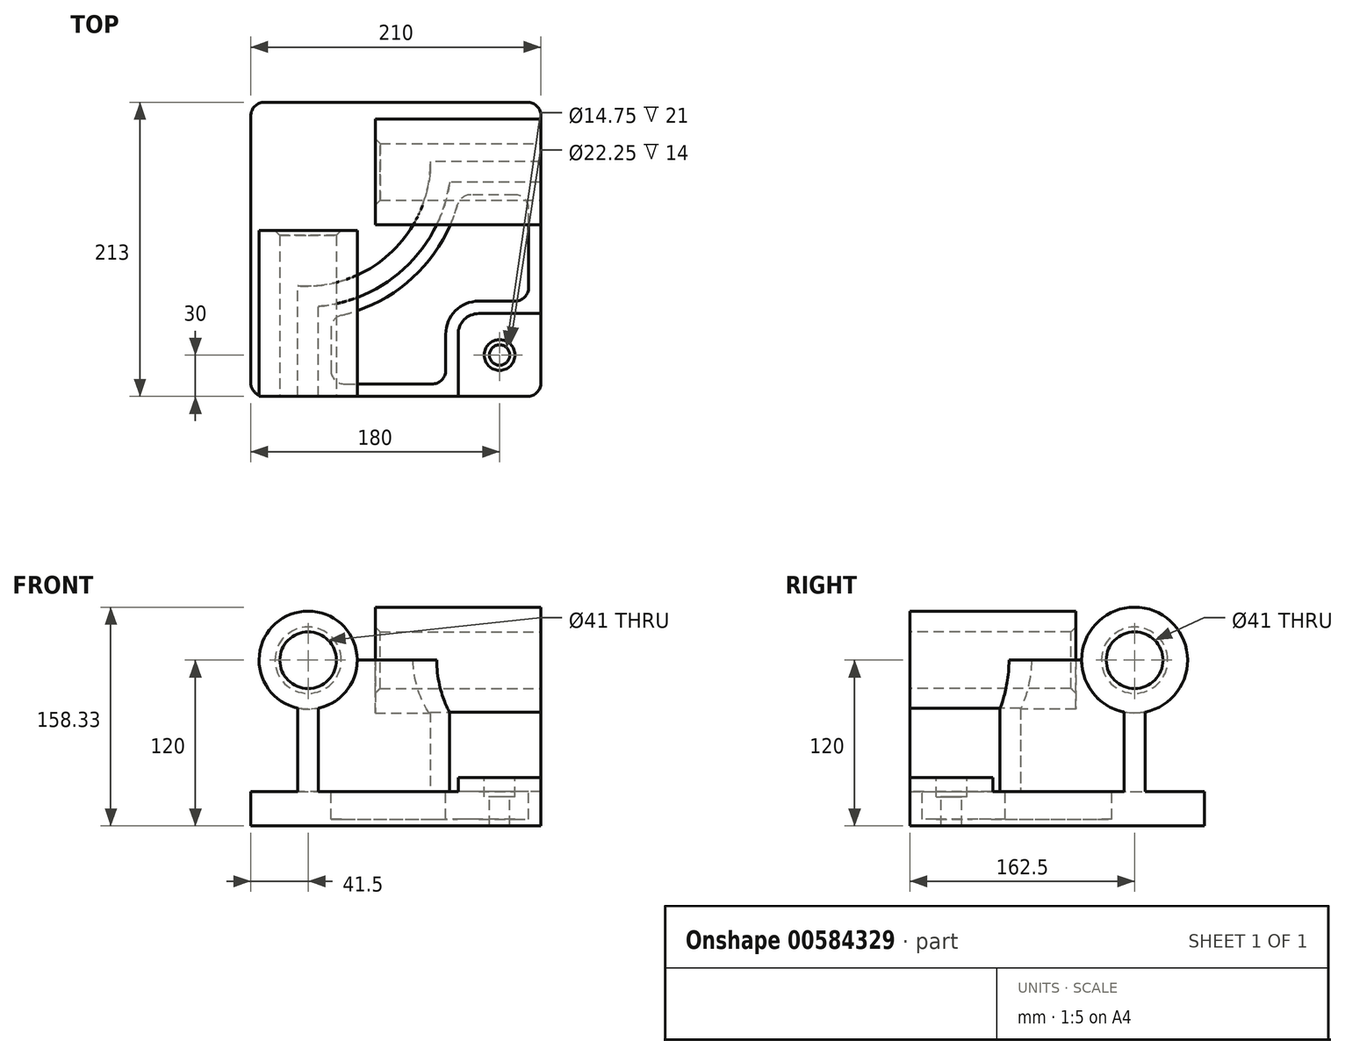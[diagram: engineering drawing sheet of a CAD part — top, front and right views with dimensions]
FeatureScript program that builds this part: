
annotation { "Feature Type Name" : "Feature", "Feature Type Description" : "" }
export const myFeature = defineFeature(function(context is Context, id is Id, definition is map)
    precondition{}
    {
        {
            var Q0;
            Q0=qCreatedBy(makeId("Top.planeOp"),FACE);
            var sketch = newSketch(context, id + "F0", { "sketchPlane" : qUnion([Q0])});
            skLineSegment(sketch, "E0.bottom", {"start": v(105, -106.5) * mm, "end": v(-105, -106.5) * mm});
            skLineSegment(sketch, "E0.top", {"start": v(105, 106.5) * mm, "end": v(-105, 106.5) * mm});
            skLineSegment(sketch, "E0.left", {"start": v(105, -106.5) * mm, "end": v(105, 106.5) * mm});
            skLineSegment(sketch, "E0.right", {"start": v(-105, -106.5) * mm, "end": v(-105, 106.5) * mm});
            skPoint(sketch, "E0.middle", {"position": v(0, 0) * mm});
            skSolve(sketch);
        }
        {
            var Q0;
            Q0=makeQuery(id+"F0.imprint","IMPRINT",FACE,{"disambiguationData":[TD([[makeQuery(id+"F0.imprint","IMPRINT",EDGE,{"derivedFrom":sQuery(id+"F0.wireOp",EDGE,"E0.bottom")}),-1.0]])]});
            extrude(context, id + "F1", {"entities" : qUnion([Q0]), "depth" : 25 * mm, "offsetDistance" : 25 * mm});
        }
        {
            var Q0;
            Q0=makeQuery(id+"F1.opExtrude","CAP_FACE",FACE,{"disambiguationData":[OSD([sQuery(id+"F0.wireOp",EDGE,"E0.bottom"),sQuery(id+"F0.wireOp",EDGE,"E0.top"),sQuery(id+"F0.wireOp",EDGE,"E0.left"),sQuery(id+"F0.wireOp",EDGE,"E0.right")])],"isStart":false});
            var sketch = newSketch(context, id + "F2", { "sketchPlane" : qUnion([Q0])});
            skLineSegment(sketch, "E1", {"start": v(-71, -106.5) * mm, "end": v(-71, -26.5) * mm});
            skLineSegment(sketch, "E2", {"start": v(105, 63.5) * mm, "end": v(25, 63.5) * mm});
            skArc(sketch, "E3", {"start": v(-71, -26.5) * mm, "mid": v(-3.5, -2.3) * mm, "end": v(25, 63.5) * mm});
            skLineSegment(sketch, "E4", {"start": v(25, 63.5) * mm, "end": v(-65.19, 63.5) * mm, "construction": true});
            skLineSegment(sketch, "E5", {"start": v(-71, -26.5) * mm, "end": v(-65.19, 63.5) * mm, "construction": true});
            skLineSegment(sketch, "E6.0", {"start": v(-56, -106.5) * mm, "end": v(-56, -41.29) * mm});
            skArc(sketch, "E6.1", {"start": v(-56, -41.29) * mm, "mid": v(7.1, -12.92) * mm, "end": v(38.92, 48.5) * mm});
            skLineSegment(sketch, "E6.2", {"start": v(105, 48.5) * mm, "end": v(38.92, 48.5) * mm});
            skSolve(sketch);
        }
        {
            var Q0;
            {var subQ4=sQuery(id+"F2.wireOp",EDGE,"E1");Q0=makeQuery(id+"F2.imprint","IMPRINT",FACE,{"disambiguationData":[TD([[makeQuery(id+"F2.imprint","IMPRINT",EDGE,{"derivedFrom":subQ4}),-1.0]])]});}
            extrude(context, id + "F3", {"entities" : qUnion([Q0]), "operationType" : NewBodyOperationType.ADD, "depth" : 95 * mm, "offsetDistance" : 25 * mm});
        }
        {
            var Q0;
            {var subQ0=sQuery(id+"F0.wireOp",EDGE,"E0.bottom");Q0=makeQuery(id+"F3.boolean.opBoolean","MERGE",FACE,{"derivedFrom":[makeQuery(id+"F1.opExtrude","SWEPT_FACE",FACE,{"disambiguationData":[OSD([subQ0])]}),makeQuery(id+"F3.opExtrude","SWEPT_FACE",FACE,{"disambiguationData":[OSD([subQ0])]})]});}
            var sketch = newSketch(context, id + "F4", { "sketchPlane" : qUnion([Q0])});
            skCircle(sketch, "E7", {"center": v(-63.5, 120) * mm, "radius": 35.5 * mm});
            skSolve(sketch);
        }
        {
            var Q0;
            Q0 = qSketchRegion(id + "F4", true);
            extrude(context, id + "F5", {"entities" : qUnion([Q0]), "operationType" : NewBodyOperationType.ADD, "depth" : 0 * mm, "offsetDistance" : 25 * mm, "hasSecondDirection" : true, "secondDirectionOppositeDirection" : true, "secondDirectionDepth" : 120 * mm});
        }
        {
            var Q0;
            {var subQ0=sQuery(id+"F0.wireOp",EDGE,"E0.left");Q0=makeQuery(id+"F3.boolean.opBoolean","MERGE",FACE,{"derivedFrom":[makeQuery(id+"F1.opExtrude","SWEPT_FACE",FACE,{"disambiguationData":[OSD([subQ0])]}),makeQuery(id+"F3.opExtrude","SWEPT_FACE",FACE,{"disambiguationData":[OSD([subQ0])]})]});}
            var sketch = newSketch(context, id + "F6", { "sketchPlane" : qUnion([Q0])});
            skCircle(sketch, "E8", {"center": v(56, 120) * mm, "radius": 38.33 * mm});
            skSolve(sketch);
        }
        {
            var Q0;
            Q0 = qSketchRegion(id + "F6", true);
            extrude(context, id + "F7", {"entities" : qUnion([Q0]), "operationType" : NewBodyOperationType.ADD, "depth" : 0 * mm, "offsetDistance" : 25 * mm, "hasSecondDirection" : true, "secondDirectionOppositeDirection" : true, "secondDirectionDepth" : 120 * mm});
        }
        {
            var Q0;
            {var subQ0=sQuery(id+"F0.wireOp",EDGE,"E0.left");var subQ1=sQuery(id+"F0.wireOp",EDGE,"E0.bottom");Q0=makeQuery(id+"F3.boolean.opBoolean","SPLIT",FACE,{"disambiguationData":[TD([makeQuery(id+"F3.opExtrude","SWEPT_FACE",FACE,{"disambiguationData":[OSD([sQuery(id+"F2.wireOp",EDGE,"E6.0")])]})])],"derivedFrom":makeQuery(id+"F1.opExtrude","CAP_FACE",FACE,{"disambiguationData":[OSD([subQ1,sQuery(id+"F0.wireOp",EDGE,"E0.top"),subQ0,sQuery(id+"F0.wireOp",EDGE,"E0.right")])],"isStart":false})});}
            var sketch = newSketch(context, id + "F8", { "sketchPlane" : qUnion([Q0])});
            skLineSegment(sketch, "E9.bottom", {"start": v(105, -106.5) * mm, "end": v(45, -106.5) * mm});
            skLineSegment(sketch, "E9.top", {"start": v(105, -46.5) * mm, "end": v(45, -46.5) * mm});
            skLineSegment(sketch, "E9.left", {"start": v(105, -106.5) * mm, "end": v(105, -46.5) * mm});
            skLineSegment(sketch, "E9.right", {"start": v(45, -106.5) * mm, "end": v(45, -46.5) * mm});
            skSolve(sketch);
        }
        {
            var Q0;
            Q0 = qSketchRegion(id + "F8", true);
            extrude(context, id + "F9", {"entities" : qUnion([Q0]), "operationType" : NewBodyOperationType.ADD, "depth" : 10 * mm, "offsetDistance" : 25 * mm});
        }
        {
            var Q0;
            Q0=makeQuery(id+"F9.opExtrude","SWEPT_EDGE",EDGE,{"disambiguationData":[OSD([sQuery(id+"F8.wireOp",EDGE,"E9.top"),sQuery(id+"F8.wireOp",EDGE,"E9.right")])]});
            fillet(context, id + "F10", {"entities" : qUnion([Q0]), "radius" : 15 * mm, "tangentPropagation" : true, "allowEdgeOverflow" : false});
        }
        {
            var Q0;
            {var subQ0=sQuery(id+"F0.wireOp",EDGE,"E0.left");var subQ1=sQuery(id+"F0.wireOp",EDGE,"E0.bottom");Q0=makeQuery(id+"F3.boolean.opBoolean","SPLIT",FACE,{"disambiguationData":[TD([makeQuery(id+"F3.opExtrude","SWEPT_FACE",FACE,{"disambiguationData":[OSD([sQuery(id+"F2.wireOp",EDGE,"E6.0")])]})])],"derivedFrom":makeQuery(id+"F1.opExtrude","CAP_FACE",FACE,{"disambiguationData":[OSD([subQ1,sQuery(id+"F0.wireOp",EDGE,"E0.top"),subQ0,sQuery(id+"F0.wireOp",EDGE,"E0.right")])],"isStart":false})});}
            var sketch = newSketch(context, id + "F11", { "sketchPlane" : qUnion([Q0])});
            skLineSegment(sketch, "E10.0", {"start": v(-47, -49.23) * mm, "end": v(-47, -97.5) * mm});
            skArc(sketch, "E10.1", {"start": v(46.45, 39.5) * mm, "mid": v(13.44, -19.3) * mm, "end": v(-47, -49.23) * mm});
            skLineSegment(sketch, "E10.2", {"start": v(-47, -97.5) * mm, "end": v(36, -97.5) * mm});
            skLineSegment(sketch, "E10.3", {"start": v(96, 39.5) * mm, "end": v(46.45, 39.5) * mm});
            skLineSegment(sketch, "E10.4", {"start": v(36, -97.5) * mm, "end": v(36, -61.5) * mm});
            skArc(sketch, "E10.5", {"start": v(36, -61.5) * mm, "mid": v(43.03, -44.53) * mm, "end": v(60, -37.5) * mm});
            skLineSegment(sketch, "E10.6", {"start": v(60, -37.5) * mm, "end": v(96, -37.5) * mm});
            skLineSegment(sketch, "E10.7", {"start": v(96, -37.5) * mm, "end": v(96, 39.5) * mm});
            skSolve(sketch);
        }
        {
            var Q0;
            Q0=makeQuery(id+"F11.imprint","IMPRINT",FACE,{"disambiguationData":[TD([[makeQuery(id+"F11.imprint","IMPRINT",EDGE,{"derivedFrom":sQuery(id+"F11.wireOp",EDGE,"E10.0")}),1.0]])]});
            extrude(context, id + "F12", {"entities" : qUnion([Q0]), "operationType" : NewBodyOperationType.REMOVE, "oppositeDirection" : true, "depth" : 20 * mm, "offsetDistance" : 25 * mm});
        }
        {
            var Q0;
            Q0=makeQuery(id+"F9.opExtrude","CAP_FACE",FACE,{"disambiguationData":[OSD([sQuery(id+"F8.wireOp",EDGE,"E9.bottom"),sQuery(id+"F8.wireOp",EDGE,"E9.top"),sQuery(id+"F8.wireOp",EDGE,"E9.left"),sQuery(id+"F8.wireOp",EDGE,"E9.right")])],"isStart":false});
            var sketch = newSketch(context, id + "F13", { "sketchPlane" : qUnion([Q0])});
            skCircle(sketch, "E11", {"center": v(75, -76.5) * mm, "radius": 15 * mm});
            skSolve(sketch);
        }
        {
            var Q0;
            Q0=sQuery(id+"F13.wireOp",VERTEX,"E11.center");
            var Q1;
            Q1=makeQuery(id+"F1.opExtrude","SWEPT_BODY",BODY,{"disambiguationData":[OSD([sQuery(id+"F0.wireOp",EDGE,"E0.bottom"),sQuery(id+"F0.wireOp",EDGE,"E0.top"),sQuery(id+"F0.wireOp",EDGE,"E0.left"),sQuery(id+"F0.wireOp",EDGE,"E0.right")])]});
            hole(context, id + "F14", {"style" : HoleStyle.C_BORE, "endStyle" : HoleEndStyle.THROUGH, "standardTappedOrClearance" : lookupTablePath({ "standard" : "ISO", "fit" : "Close", "size" : "M14", "type" : "Clearance" }), "standardBlindInLast" : lookupTablePath({ "fit" : "Close", "standard" : "ISO", "size" : "M14", "type" : "Clearance" }), "holeDiameter" : 14.75 * mm, "cBoreDiameter" : 22.25 * mm, "cBoreDepth" : 14 * mm, "majorDiameter" : 5 * mm, "isTappedThrough" : true, "tappedDepth" : 12 * mm, "tapClearance" : 3, "locations" : qUnion([Q0]), "scope" : qUnion([Q1])});
        }
        {
            var Q0;
            Q0=makeQuery(id+"F12.boolean.opBoolean","COPY",EDGE,{"derivedFrom":makeQuery(id+"F12.opExtrude","SWEPT_EDGE",EDGE,{"disambiguationData":[OSD([sQuery(id+"F11.wireOp",EDGE,"E10.0"),sQuery(id+"F11.wireOp",EDGE,"E10.1")])]})});
            var Q1;
            Q1=makeQuery(id+"F12.boolean.opBoolean","COPY",EDGE,{"derivedFrom":makeQuery(id+"F12.opExtrude","SWEPT_EDGE",EDGE,{"disambiguationData":[OSD([sQuery(id+"F11.wireOp",EDGE,"E10.1"),sQuery(id+"F11.wireOp",EDGE,"E10.3")])]})});
            var Q2;
            Q2=makeQuery(id+"F12.boolean.opBoolean","COPY",EDGE,{"derivedFrom":makeQuery(id+"F12.opExtrude","SWEPT_EDGE",EDGE,{"disambiguationData":[OSD([sQuery(id+"F11.wireOp",EDGE,"E10.3"),sQuery(id+"F11.wireOp",EDGE,"E10.7")])]})});
            var Q3;
            Q3=makeQuery(id+"F12.boolean.opBoolean","COPY",EDGE,{"derivedFrom":makeQuery(id+"F12.opExtrude","SWEPT_EDGE",EDGE,{"disambiguationData":[OSD([sQuery(id+"F11.wireOp",EDGE,"E10.0"),sQuery(id+"F11.wireOp",EDGE,"E10.2")])]})});
            var Q4;
            Q4=makeQuery(id+"F12.boolean.opBoolean","COPY",EDGE,{"derivedFrom":makeQuery(id+"F12.opExtrude","SWEPT_EDGE",EDGE,{"disambiguationData":[OSD([sQuery(id+"F11.wireOp",EDGE,"E10.2"),sQuery(id+"F11.wireOp",EDGE,"E10.4")])]})});
            var Q5;
            Q5=makeQuery(id+"F12.boolean.opBoolean","COPY",EDGE,{"derivedFrom":makeQuery(id+"F12.opExtrude","SWEPT_EDGE",EDGE,{"disambiguationData":[OSD([sQuery(id+"F11.wireOp",EDGE,"E10.6"),sQuery(id+"F11.wireOp",EDGE,"E10.7")])]})});
            fillet(context, id + "F15", {"entities" : qUnion([Q0, Q1, Q2, Q3, Q4, Q5]), "radius" : 10 * mm, "tangentPropagation" : true, "allowEdgeOverflow" : false});
        }
        {
            var Q0;
            Q0=makeQuery(id+"F5.opExtrude","CAP_FACE",FACE,{"disambiguationData":[OSD([sQuery(id+"F4.wireOp",EDGE,"E7")])],"isStart":false});
            var sketch = newSketch(context, id + "F16", { "sketchPlane" : qUnion([Q0])});
            skCircle(sketch, "E12", {"center": v(-63.5, 120) * mm, "radius": 20.5 * mm});
            skSolve(sketch);
        }
        {
            var Q0;
            Q0=makeQuery(id+"F16.imprint","IMPRINT",FACE,{"disambiguationData":[TD([[makeQuery(id+"F16.imprint","IMPRINT",EDGE,{"derivedFrom":sQuery(id+"F16.wireOp",EDGE,"E12")}),1.0]])]});
            var Q1;
            Q1 = qConstructionFilter(qBodyType(qCreatedBy(id + "F16" ,EDGE), BodyType.WIRE), ConstructionObject.NO);
            extrude(context, id + "F17", {"entities" : qUnion([Q0]), "operationType" : NewBodyOperationType.REMOVE, "surfaceEntities" : qUnion([Q1]), "endBound" : BoundingType.THROUGH_ALL, "oppositeDirection" : true, "depth" : 25 * mm, "offsetDistance" : 25 * mm});
        }
        {
            var Q0;
            Q0=makeQuery(id+"F7.opExtrude","CAP_FACE",FACE,{"disambiguationData":[OSD([sQuery(id+"F6.wireOp",EDGE,"E8")])],"isStart":false});
            var sketch = newSketch(context, id + "F18", { "sketchPlane" : qUnion([Q0])});
            skCircle(sketch, "E13", {"center": v(56, 120) * mm, "radius": 20.5 * mm});
            skSolve(sketch);
        }
        {
            var Q0;
            Q0 = qSketchRegion(id + "F18", true);
            extrude(context, id + "F19", {"entities" : qUnion([Q0]), "operationType" : NewBodyOperationType.REMOVE, "endBound" : BoundingType.THROUGH_ALL, "oppositeDirection" : true, "depth" : 25 * mm, "offsetDistance" : 25 * mm});
        }
        {
            var Q0;
            Q0=makeQuery(id+"F17.boolean.opBoolean","COPY",EDGE,{"derivedFrom":makeQuery(id+"F17.opExtrude","CAP_EDGE",EDGE,{"disambiguationData":[OSD([sQuery(id+"F16.wireOp",EDGE,"E12")])],"isStart":true})});
            var Q1;
            Q1=makeQuery(id+"F19.boolean.opBoolean","COPY",EDGE,{"derivedFrom":makeQuery(id+"F19.opExtrude","CAP_EDGE",EDGE,{"disambiguationData":[OSD([sQuery(id+"F18.wireOp",EDGE,"E13")])],"isStart":true})});
            var Q2;
            Q2=makeQuery(id+"F17.boolean.opBoolean","INTERSECT",EDGE,{"derivedFrom":[makeQuery(id+"F5.opExtrude","CAP_FACE",FACE,{"disambiguationData":[OSD([sQuery(id+"F4.wireOp",EDGE,"E7")])],"isStart":true}),makeQuery(id+"F17.opExtrude","SWEPT_FACE",FACE,{"disambiguationData":[OSD([sQuery(id+"F16.wireOp",EDGE,"E12")])]})]});
            var Q3;
            Q3=makeQuery(id+"F19.boolean.opBoolean","INTERSECT",EDGE,{"derivedFrom":[makeQuery(id+"F7.opExtrude","CAP_FACE",FACE,{"disambiguationData":[OSD([sQuery(id+"F6.wireOp",EDGE,"E8")])],"isStart":true}),makeQuery(id+"F19.opExtrude","SWEPT_FACE",FACE,{"disambiguationData":[OSD([sQuery(id+"F18.wireOp",EDGE,"E13")])]})]});
            chamfer(context, id + "F20", {"entities" : qUnion([Q0, Q1, Q2, Q3]), "width" : 3.5 * mm, "tangentPropagation" : true});
        }
        {
            var Q0;
            Q0=makeQuery(id+"F9.boolean.opBoolean","MERGE",EDGE,{"derivedFrom":[makeQuery(id+"F1.opExtrude","SWEPT_EDGE",EDGE,{"disambiguationData":[OSD([sQuery(id+"F0.wireOp",EDGE,"E0.bottom"),sQuery(id+"F0.wireOp",EDGE,"E0.left")])]}),makeQuery(id+"F9.opExtrude","SWEPT_EDGE",EDGE,{"disambiguationData":[OSD([sQuery(id+"F8.wireOp",EDGE,"E9.bottom"),sQuery(id+"F8.wireOp",EDGE,"E9.left")])]})]});
            var Q1;
            Q1=makeQuery(id+"F1.opExtrude","SWEPT_EDGE",EDGE,{"disambiguationData":[OSD([sQuery(id+"F0.wireOp",EDGE,"E0.bottom"),sQuery(id+"F0.wireOp",EDGE,"E0.right")])]});
            var Q2;
            Q2=makeQuery(id+"F1.opExtrude","SWEPT_EDGE",EDGE,{"disambiguationData":[OSD([sQuery(id+"F0.wireOp",EDGE,"E0.top"),sQuery(id+"F0.wireOp",EDGE,"E0.left")])]});
            var Q3;
            Q3=makeQuery(id+"F1.opExtrude","SWEPT_EDGE",EDGE,{"disambiguationData":[OSD([sQuery(id+"F0.wireOp",EDGE,"E0.top"),sQuery(id+"F0.wireOp",EDGE,"E0.right")])]});
            fillet(context, id + "F21", {"entities" : qUnion([Q0, Q1, Q2, Q3]), "radius" : 10 * mm, "tangentPropagation" : true, "allowEdgeOverflow" : false});
        }
    });
